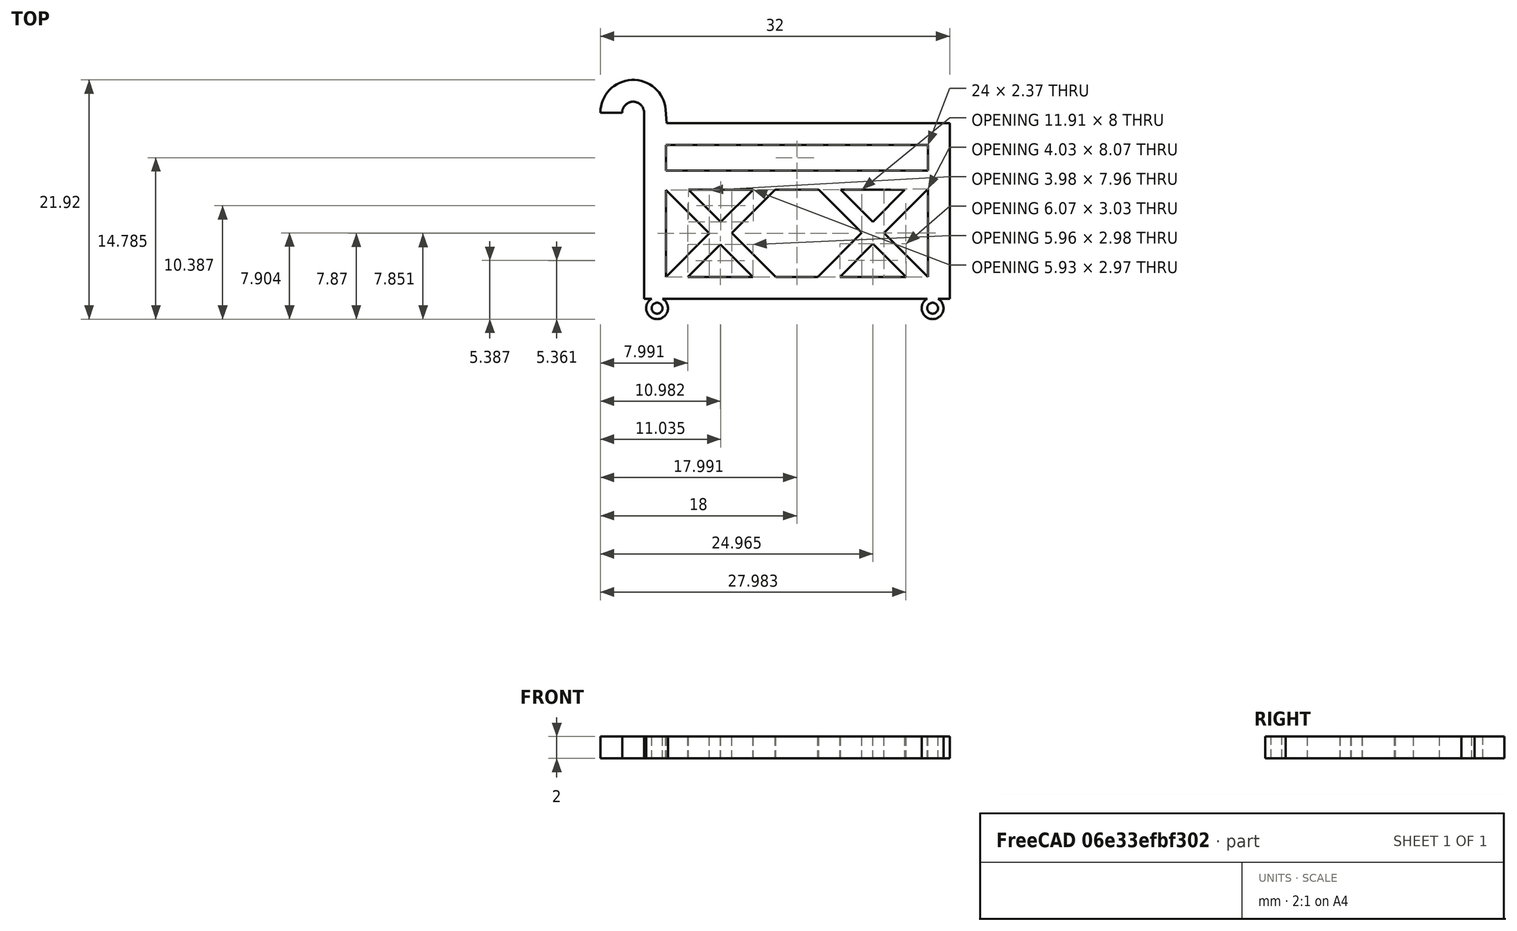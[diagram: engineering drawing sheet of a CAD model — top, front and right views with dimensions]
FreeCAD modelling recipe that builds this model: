
FCSTD DOCUMENT  (FreeCAD 0.18R16131 (Git))
Label: jardiniere_elodie
License: All rights reserved
LicenseURL: http://en.wikipedia.org/wiki/All_rights_reserved
objects: Sketcher::SketchObject×1, PartDesign::Pad×1, PartDesign::Body×1
note: 4 computed .brp shape members not serialized (recipe doc carries the construction recipe); baked Part::Feature solids carry a one-line shape summary decoded from their .brp

FEATURE [Sketcher::SketchObject] Sketch
  MapMode = 5
  Support = -> [XY_Plane]
  sketch-geometry (54):
    g0: LineSegment StartX=-11.9231 StartY=6.1 StartZ=0 EndX=14 EndY=6.1 EndZ=0
    g1: LineSegment StartX=14 StartY=6.1 StartZ=0 EndX=14 EndY=-10 EndZ=0
    g2: LineSegment StartX=-14 StartY=-10 StartZ=0 EndX=-14 EndY=7.05103 EndZ=0
    g3: ArcOfCircle CenterX=-15 CenterY=7.05103 CenterZ=0 NormalX=0 NormalY=0 NormalZ=1 AngleXU=0 Radius=3 StartAngle=0.089331 EndAngle=3.14163
    g4: ArcOfCircle CenterX=-15 CenterY=7.05103 CenterZ=0 NormalX=0 NormalY=0 NormalZ=1 AngleXU=0 Radius=1 StartAngle=1.20144e-11 EndAngle=3.14172
    g5: LineSegment StartX=-18 StartY=7.0509 StartZ=0 EndX=-16 EndY=7.0509 EndZ=0
    g6: LineSegment StartX=-14 StartY=-10 StartZ=0 EndX=-13.3088 EndY=-10 EndZ=0
    g7: LineSegment StartX=-12.3088 StartY=-10 StartZ=0 EndX=11.9327 EndY=-10 EndZ=0
    g8: LineSegment StartX=12.9327 StartY=-10 StartZ=0 EndX=14 EndY=-10 EndZ=0
    g9: ArcOfCircle CenterX=-12.8088 CenterY=-10.866 CenterZ=0 NormalX=0 NormalY=0 NormalZ=1 AngleXU=0 Radius=1 StartAngle=2.0944 EndAngle=7.33038
    g10: ArcOfCircle CenterX=12.4327 CenterY=-10.866 CenterZ=0 NormalX=0 NormalY=0 NormalZ=1 AngleXU=0 Radius=1 StartAngle=2.0944 EndAngle=7.33038
    g11: Circle CenterX=-12.8088 CenterY=-10.866 CenterZ=0 NormalX=0 NormalY=0 NormalZ=1 AngleXU=0 Radius=0.5
    g12: Circle CenterX=12.4327 CenterY=-10.866 CenterZ=0 NormalX=0 NormalY=0 NormalZ=1 AngleXU=0 Radius=0.5
    g13: LineSegment StartX=-12 StartY=4.1 StartZ=0 EndX=12 EndY=4.1 EndZ=0
    g14: LineSegment StartX=12 StartY=4.1 StartZ=0 EndX=12 EndY=1.72972 EndZ=0
    g15: LineSegment StartX=-12 StartY=-8 StartZ=0 EndX=-12 EndY=-0.0370732 EndZ=0
    g16: LineSegment StartX=-12 StartY=1.72972 StartZ=0 EndX=12 EndY=1.72972 EndZ=0
    g17: LineSegment StartX=-9.93092 StartY=0 StartZ=0 EndX=-6.96546 EndY=-2.96546 EndZ=0
    g18: LineSegment StartX=-12 StartY=-0.0370732 StartZ=0 EndX=-8.01854 EndY=-4.01854 EndZ=0
    g19: LineSegment StartX=2 StartY=0 StartZ=0 EndX=5.94796 EndY=-3.94796 EndZ=0
    g20: LineSegment StartX=4 StartY=0 StartZ=0 EndX=6.94796 EndY=-2.94796 EndZ=0
    g21: LineSegment StartX=-10 StartY=-8 StartZ=0 EndX=-7.01854 EndY=-5.01854 EndZ=0
    g22: LineSegment StartX=-12 StartY=-8 StartZ=0 EndX=-8.01854 EndY=-4.01854 EndZ=0
    g23: LineSegment StartX=1.89591 StartY=-8 StartZ=0 EndX=5.94796 EndY=-3.94796 EndZ=0
    g24: LineSegment StartX=3.93088 StartY=-8 StartZ=0 EndX=6.96544 EndY=-4.96544 EndZ=0
    g25: LineSegment StartX=-9.93092 StartY=0 StartZ=0 EndX=-4 EndY=0 EndZ=0
    g26: LineSegment StartX=-2 StartY=0 StartZ=0 EndX=2 EndY=0 EndZ=0
    g27: LineSegment StartX=4 StartY=0 StartZ=0 EndX=9.89591 EndY=0 EndZ=0
    g28: LineSegment [constr] StartX=-24.5249 StartY=-8 StartZ=0 EndX=29.7131 EndY=-8 EndZ=0
    g29: LineSegment StartX=-10 StartY=-8 StartZ=0 EndX=-4.03707 EndY=-8 EndZ=0
    g30: LineSegment StartX=-1.93092 StartY=-8 StartZ=0 EndX=1.89591 EndY=-8 EndZ=0
    g31: LineSegment StartX=3.93088 StartY=-8 StartZ=0 EndX=10 EndY=-8 EndZ=0
    g32: GeomPoint X=-6.96546 Y=-2.96546 Z=0
    g33: GeomPoint X=-5.96546 Y=-3.96546 Z=0
    g34: GeomPoint X=-7.01854 Y=-5.01854 Z=0
    g35: GeomPoint X=-8.01854 Y=-4.01854 Z=0
    g36: LineSegment StartX=-5.96546 StartY=-3.96546 StartZ=0 EndX=-1.93092 EndY=-8 EndZ=0
    g37: LineSegment StartX=-7.01854 StartY=-5.01854 StartZ=0 EndX=-4.03707 EndY=-8 EndZ=0
    g38: LineSegment StartX=-5.96546 StartY=-3.96546 StartZ=0 EndX=-2 EndY=0 EndZ=0
    g39: LineSegment StartX=-6.96546 StartY=-2.96546 StartZ=0 EndX=-4 EndY=0 EndZ=0
    g40: GeomPoint X=7.96544 Y=-3.96544 Z=0
    g41: GeomPoint X=6.96544 Y=-4.96544 Z=0
    g42: GeomPoint X=5.94796 Y=-3.94796 Z=0
    g43: GeomPoint X=6.94796 Y=-2.94796 Z=0
    g44: LineSegment StartX=7.96544 StartY=-3.96544 StartZ=0 EndX=12 EndY=0.0691172 EndZ=0
    g45: LineSegment StartX=7.96544 StartY=-3.96544 StartZ=0 EndX=12 EndY=-8 EndZ=0
    g46: LineSegment StartX=6.94796 StartY=-2.94796 StartZ=0 EndX=9.89591 EndY=0 EndZ=0
    g47: LineSegment StartX=6.96544 StartY=-4.96544 StartZ=0 EndX=10 EndY=-8 EndZ=0
    g48: LineSegment StartX=-12 StartY=1.72972 StartZ=0 EndX=-12 EndY=4.1 EndZ=0
    g49: LineSegment StartX=12 StartY=0.0691172 StartZ=0 EndX=12 EndY=-8 EndZ=0
    g50: LineSegment StartX=-12.012 StartY=7.31866 StartZ=0 EndX=-11.9231 EndY=6.1 EndZ=0
    g51: LineSegment [constr] StartX=-23.8495 StartY=-10 StartZ=0 EndX=34.3969 EndY=-10 EndZ=0
    g52: GeomPoint X=-14.8924 Y=10.0491 Z=0
    g53: GeomPoint X=-12.7623 Y=-11.8649 Z=0
  constraints (127):
    c: Coincident(g0,g1)
    c: Vertical(g1)
    c: DistanceX(g2,g1) = 28
    c: Horizontal(g0)
    c: Vertical(g2)
    c: Radius(g3) = 3
    c: Coincident(g4,g3)
    c: Radius(g4) = 1
    c: Coincident(g2,g4)
    c: Coincident(g5,g3)
    c: Coincident(g5,g4)
    c: Coincident(g6,g2)
    c: Horizontal(g6)
    c: Horizontal(g7)
    c: Coincident(g8,g1)
    c: Horizontal(g8)
    c: Coincident(g9,g6)
    c: Coincident(g9,g7)
    c: Coincident(g10,g7)
    c: Coincident(g8,g10)
    c: Radius(g9) = 1
    c: Radius(g10) = 1
    c: DistanceX(g2,g-1) = 14
    c: Coincident(g11,g9)
    c: Radius(g11) = 0.5
    c: DistanceX(g6,g7) = 1
    c: DistanceX(g7,g8) = 1
    c: Coincident(g12,g10)
    c: Radius(g12) = 0.5
    c: DistanceY(g2,g-1) = 10
    c: Coincident(g13,g14)
    c: Coincident(g48,g13)
    c: Horizontal(g13)
    c: Vertical(g14)
    c: Vertical(g15)
    c: DistanceY(g13,g0) = 2
    c: DistanceX(g13,g0) = 2
    c: DistanceY(g1,g49) = 2
    c: DistanceX(g2,g15) = 2
    c: Horizontal(g16)
    c: PointOnObject(g17,g-1)
    c: Angle(g15,g18) = 0.785398
    c: Parallel(g17,g18)
    c: Parallel(g20,g19)
    c: DistanceX(g19,g20) = 2
    c: PointOnObject(g20,g-1)
    c: PointOnObject(g19,g-1)
    c: Coincident(g45,g49)
    c: Angle(g20,g-1) = 0.785398
    c: PointOnObject(g38,g-1)
    c: Angle(g21) = 0.785398
    c: Parallel(g21,g22) = 0.785398
    c: PointOnObject(g39,g-1)
    c: DistanceX(g39,g38) = 2
    c: Parallel(g21,g24) = 0.785398
    c: Parallel(g24,g23) = 0.785398
    c: PointOnObject(g46,g-1)
    c: Coincident(g25,g17)
    c: Coincident(g25,g39)
    c: Coincident(g26,g38)
    c: Coincident(g26,g19)
    c: Coincident(g27,g20)
    c: Coincident(g27,g46)
    c: Horizontal(g28)
    c: PointOnObject(g49,g28)
    c: PointOnObject(g23,g28)
    c: PointOnObject(g24,g28)
    c: PointOnObject(g36,g28)
    c: PointOnObject(g37,g28)
    c: PointOnObject(g21,g28)
    c: Coincident(g29,g21)
    c: Coincident(g29,g37)
    c: Coincident(g30,g36)
    c: Coincident(g30,g23)
    c: Coincident(g31,g24)
    c: Coincident(g31,g47)
    c: Horizontal(g31)
    c: PointOnObject(g32,g22)
    c: PointOnObject(g32,g17)
    c: PointOnObject(g33,g17)
    c: PointOnObject(g34,g18)
    c: PointOnObject(g35,g22)
    c: PointOnObject(g33,g21)
    c: Coincident(g22,g15)
    c: PointOnObject(g15,g28)
    c: PointOnObject(g34,g21)
    c: PointOnObject(g35,g18)
    c: Tangent(g17,g36)
    c: Tangent(g18,g37)
    c: Coincident(g21,g37)
    c: Coincident(g38,g36)
    c: Tangent(g21,g38)
    c: Coincident(g22,g18)
    c: Coincident(g39,g17)
    c: Tangent(g22,g39)
    c: PointOnObject(g40,g20)
    c: PointOnObject(g42,g23)
    c: PointOnObject(g43,g20)
    c: PointOnObject(g43,g23)
    c: PointOnObject(g42,g19)
    c: PointOnObject(g40,g24)
    c: PointOnObject(g41,g19)
    c: PointOnObject(g41,g24)
    c: Tangent(g24,g44)
    c: Coincident(g45,g44)
    c: Tangent(g20,g45)
    c: Coincident(g46,g20)
    c: Tangent(g23,g46)
    c: Coincident(g19,g23)
    c: Coincident(g47,g24)
    c: Tangent(g19,g47)
    c: Coincident(g15,g18)
    c: Coincident(g48,g16)
    c: Tangent(g15,g48)
    c: Coincident(g14,g16)
    c: Coincident(g49,g44)
    c: Tangent(g14,g49)
    c: Horizontal(g5)
    c: Coincident(g50,g3)
    c: Coincident(g50,g0)
    c: Horizontal(g51)
    c: PointOnObject(g2,g51)
    c: PointOnObject(g7,g51)
    c: PointOnObject(g53,g9)
    c: PointOnObject(g1,g51)
    c: PointOnObject(g52,g3)
    c: DistanceY(g1,g0) = 16.1
FEATURE [PartDesign::Pad] Pad
  Length = 2
  Length2 = 100
  Profile = -> Sketch
  Type = 0
FEATURE [PartDesign::Body] Body
  Group = -> [Sketch,Pad]
  Origin = -> Origin
  Tip = -> Pad
